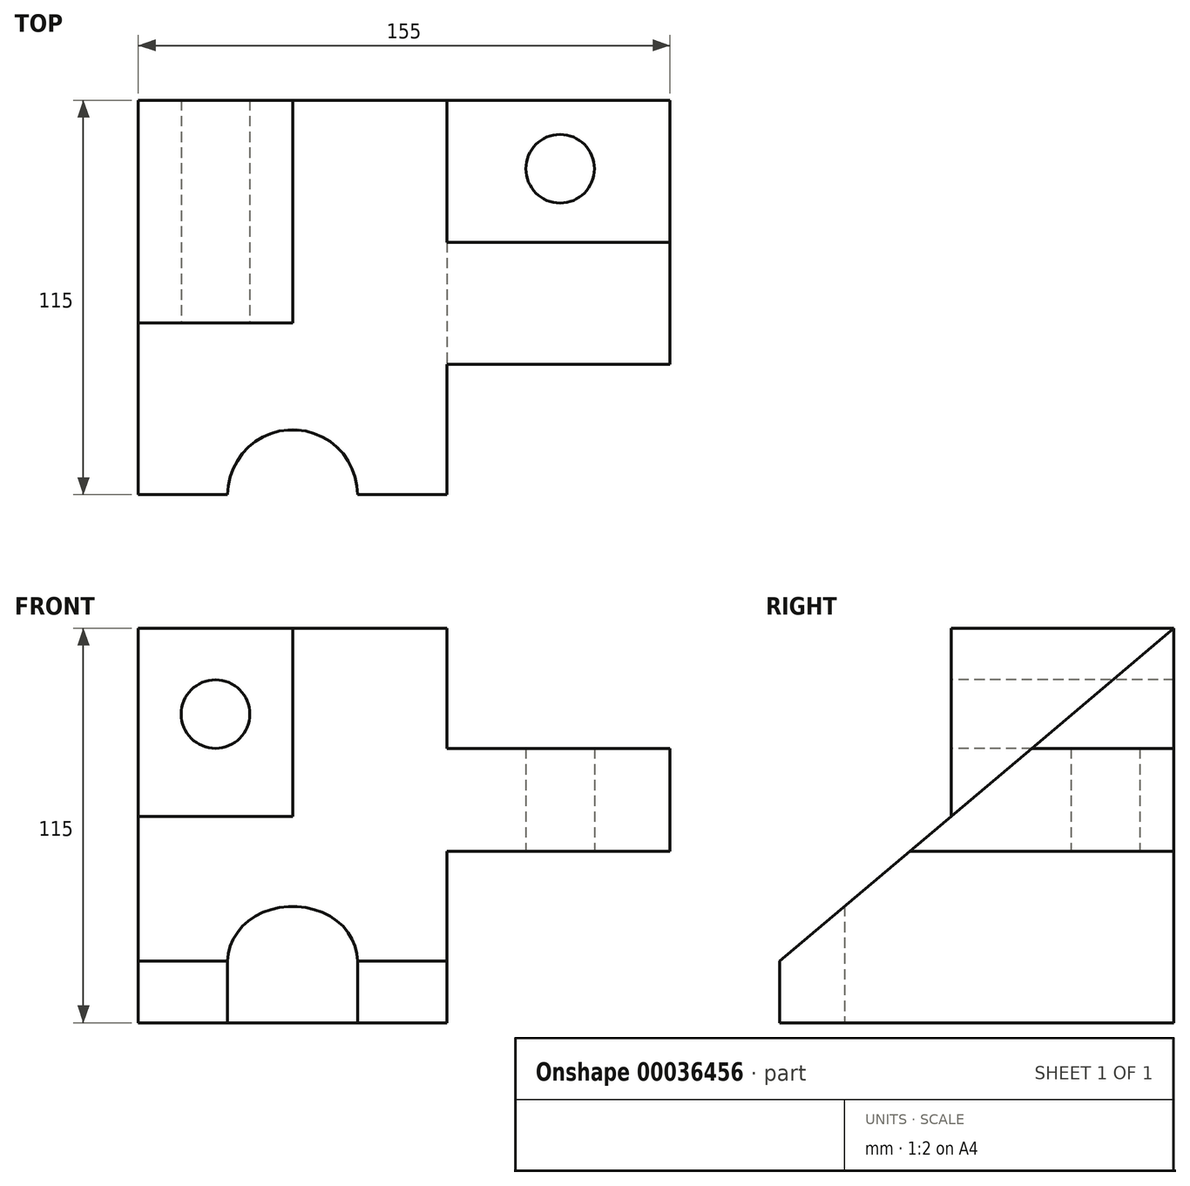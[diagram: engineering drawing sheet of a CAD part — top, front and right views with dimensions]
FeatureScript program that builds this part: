
annotation { "Feature Type Name" : "Feature", "Feature Type Description" : "" }
export const myFeature = defineFeature(function(context is Context, id is Id, definition is map)
    precondition{}
    {
        {
            var Q0;
            Q0=qCreatedBy(makeId("Right.planeOp"),FACE);
            var sketch = newSketch(context, id + "F0", { "sketchPlane" : qUnion([Q0])});
            skLineSegment(sketch, "E0", {"start": v(57.5, 0) * mm, "end": v(-57.5, 0) * mm});
            skLineSegment(sketch, "E1", {"start": v(-57.5, 0) * mm, "end": v(-57.5, 18) * mm});
            skLineSegment(sketch, "E2", {"start": v(-57.5, 18) * mm, "end": v(57.5, 115) * mm});
            skLineSegment(sketch, "E3", {"start": v(57.5, 115) * mm, "end": v(57.5, 0) * mm});
            skSolve(sketch);
        }
        {
            var Q0;
            Q0=makeQuery(id+"F0.imprint","IMPRINT",FACE,{"disambiguationData":[TD([[makeQuery(id+"F0.imprint","IMPRINT",EDGE,{"derivedFrom":sQuery(id+"F0.wireOp",EDGE,"E0")}),-1.0]])]});
            extrude(context, id + "F1", {"entities" : qUnion([Q0]), "endBound" : BoundingType.SYMMETRIC, "depth" : (90 + 65) * mm});
        }
        {
            var Q0;
            Q0=qCreatedBy(makeId("Front.planeOp"),FACE);
            var sketch = newSketch(context, id + "F2", { "sketchPlane" : qUnion([Q0])});
            skLineSegment(sketch, "E4.bottom", {"start": v(12.5, 115) * mm, "end": v(77.5, 115) * mm});
            skLineSegment(sketch, "E4.top", {"start": v(12.5, 80) * mm, "end": v(77.5, 80) * mm});
            skLineSegment(sketch, "E4.left", {"start": v(12.5, 115) * mm, "end": v(12.5, 80) * mm});
            skLineSegment(sketch, "E4.right", {"start": v(77.5, 115) * mm, "end": v(77.5, 80) * mm});
            skLineSegment(sketch, "E5.bottom", {"start": v(12.5, 50) * mm, "end": v(77.5, 50) * mm});
            skLineSegment(sketch, "E5.top", {"start": v(12.5, 0) * mm, "end": v(77.5, 0) * mm});
            skLineSegment(sketch, "E5.left", {"start": v(12.5, 50) * mm, "end": v(12.5, 0) * mm});
            skLineSegment(sketch, "E5.right", {"start": v(77.5, 50) * mm, "end": v(77.5, 0) * mm});
            skSolve(sketch);
        }
        {
            var Q0;
            Q0 = qSketchRegion(id + "F2", true);
            extrude(context, id + "F3", {"entities" : qUnion([Q0]), "operationType" : NewBodyOperationType.REMOVE, "endBound" : BoundingType.SYMMETRIC, "oppositeDirection" : true, "depth" : 200 * mm});
        }
        {
            var Q0;
            Q0=qCreatedBy(makeId("Top.planeOp"),FACE);
            var sketch = newSketch(context, id + "F4", { "sketchPlane" : qUnion([Q0])});
            skCircle(sketch, "E6", {"center": v(45.5, 37.5) * mm, "radius": 10 * mm});
            skCircle(sketch, "E7", {"center": v(-32.5, -57.5) * mm, "radius": 19 * mm});
            skSolve(sketch);
        }
        {
            var Q0;
            Q0=makeQuery(id+"F4.imprint","IMPRINT",FACE,{"disambiguationData":[TD([[makeQuery(id+"F4.imprint","IMPRINT",EDGE,{"derivedFrom":sQuery(id+"F4.wireOp",EDGE,"E7")}),1.0]])]});
            var Q1;
            Q1=makeQuery(id+"F4.imprint","IMPRINT",FACE,{"disambiguationData":[TD([[makeQuery(id+"F4.imprint","IMPRINT",EDGE,{"derivedFrom":sQuery(id+"F4.wireOp",EDGE,"E6")}),1.0]])]});
            extrude(context, id + "F5", {"entities" : qUnion([Q0, Q1]), "operationType" : NewBodyOperationType.REMOVE, "depth" : 160.94 * mm});
        }
        {
            var Q0;
            Q0=makeQuery(id+"F1.opExtrude","CAP_FACE",FACE,{"disambiguationData":[OSD([sQuery(id+"F0.wireOp",EDGE,"E0"),sQuery(id+"F0.wireOp",EDGE,"E1"),sQuery(id+"F0.wireOp",EDGE,"E2"),sQuery(id+"F0.wireOp",EDGE,"E3")])],"isStart":true});
            var sketch = newSketch(context, id + "F6", { "sketchPlane" : qUnion([Q0])});
            skLineSegment(sketch, "E8", {"start": v(-57.5, 115) * mm, "end": v(7.5, 60.17) * mm});
            skLineSegment(sketch, "E9", {"start": v(7.5, 60.17) * mm, "end": v(7.5, 115) * mm});
            skLineSegment(sketch, "E10", {"start": v(7.5, 115) * mm, "end": v(-57.5, 115) * mm});
            skSolve(sketch);
        }
        {
            var Q0;
            Q0=makeQuery(id+"F6.imprint","IMPRINT",FACE,{"disambiguationData":[TD([[makeQuery(id+"F6.imprint","IMPRINT",EDGE,{"derivedFrom":sQuery(id+"F6.wireOp",EDGE,"E8")}),-1.0]])]});
            extrude(context, id + "F7", {"entities" : qUnion([Q0]), "operationType" : NewBodyOperationType.ADD, "oppositeDirection" : true, "depth" : 45 * mm});
        }
        {
            var Q0;
            Q0=makeQuery(id+"F7.opExtrude","SWEPT_FACE",FACE,{"disambiguationData":[OSD([sQuery(id+"F6.wireOp",EDGE,"E9")])]});
            var sketch = newSketch(context, id + "F8", { "sketchPlane" : qUnion([Q0])});
            skCircle(sketch, "E11", {"center": v(-55, 90) * mm, "radius": 10 * mm});
            skSolve(sketch);
        }
        {
            var Q0;
            Q0=makeQuery(id+"F8.imprint","IMPRINT",FACE,{"disambiguationData":[TD([[makeQuery(id+"F8.imprint","IMPRINT",EDGE,{"derivedFrom":sQuery(id+"F8.wireOp",EDGE,"E11")}),1.0]])]});
            var Q1;
            Q1=sQuery(id+"F8.wireOp",EDGE,"E11");
            var Q2;
            Q2=makeQuery(id+"F1.opExtrude","SWEPT_FACE",FACE,{"disambiguationData":[OSD([sQuery(id+"F0.wireOp",EDGE,"E3")])]});
            extrude(context, id + "F9", {"entities" : qUnion([Q0]), "operationType" : NewBodyOperationType.REMOVE, "surfaceEntities" : qUnion([Q1]), "endBound" : BoundingType.UP_TO_SURFACE, "oppositeDirection" : true, "endBoundEntityFace" : qUnion([Q2]), "depth" : 25 * mm});
        }
    });
